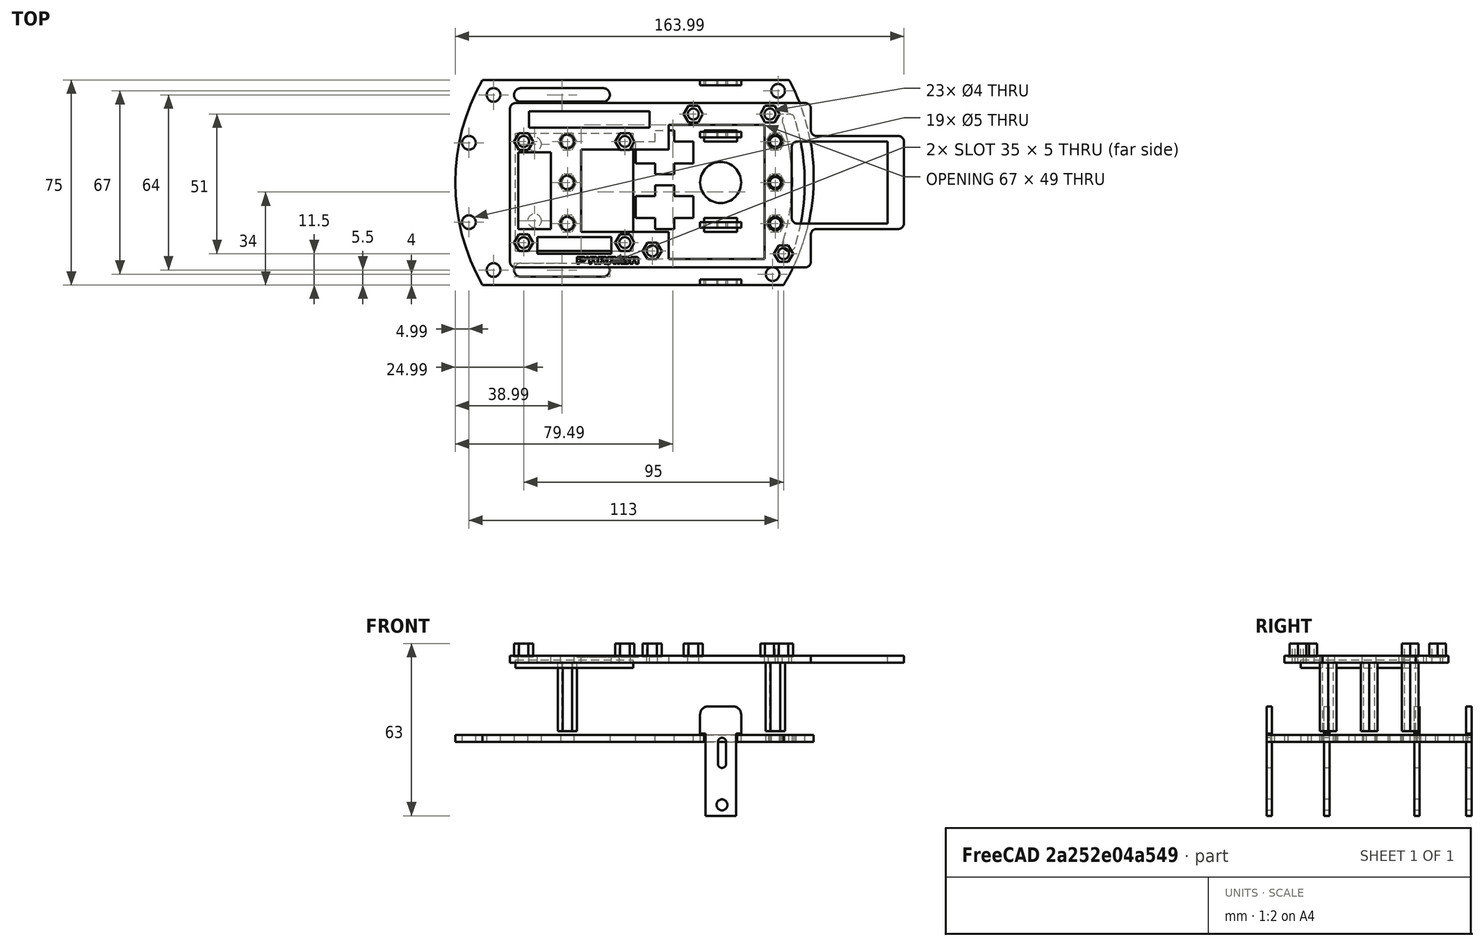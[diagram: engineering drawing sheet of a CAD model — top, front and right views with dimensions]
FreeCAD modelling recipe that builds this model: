
FCSTD DOCUMENT  (FreeCAD 0.17R13541 (Git))
Label: masayloChino2020
License: All rights reserved
LicenseURL: http://en.wikipedia.org/wiki/All_rights_reserved
objects: Part::Cylinder×41, Part::Cut×30, Part::Box×21, Part::Feature×18, Part::MultiFuse×16, Part::Prism×15, Part::Extrusion×15, Part::Fillet×6, Mesh::Feature×4, Sketcher::SketchObject×1, PartDesign::Pad×1, PartDesign::Body×1, Part::FeaturePython×1
note: 167 computed .brp shape members not serialized (recipe doc carries the construction recipe); baked Part::Feature solids carry a one-line shape summary decoded from their .brp

FEATURE [Sketcher::SketchObject] Sketch
  MapMode = 5
  Support = -> [XY_Plane]
  sketch-geometry (71):
    g0: LineSegment StartX=0 StartY=37.5 StartZ=0 EndX=81 EndY=37.5 EndZ=0
    g1: LineSegment StartX=110 StartY=-37.5 StartZ=0 EndX=93 EndY=-37.5 EndZ=0
    g2: Circle CenterX=4 CenterY=-32 CenterZ=0 NormalX=0 NormalY=0 NormalZ=1 AngleXU=0 Radius=2.5
    g3: ArcOfCircle CenterX=14 CenterY=-32 CenterZ=0 NormalX=0 NormalY=0 NormalZ=1 AngleXU=0 Radius=2.5 StartAngle=1.5708 EndAngle=4.71239
    g4: ArcOfCircle CenterX=44 CenterY=-32 CenterZ=0 NormalX=0 NormalY=0 NormalZ=1 AngleXU=0 Radius=2.5 StartAngle=4.71239 EndAngle=7.85398
    g5: LineSegment StartX=14 StartY=-34.5 StartZ=0 EndX=44 EndY=-34.5 EndZ=0
    g6: LineSegment StartX=14 StartY=-29.5 StartZ=0 EndX=44 EndY=-29.5 EndZ=0
    g7: Circle CenterX=-5 CenterY=-14.5 CenterZ=0 NormalX=0 NormalY=0 NormalZ=1 AngleXU=0 Radius=2.5
    g8: Circle CenterX=-5 CenterY=14.5 CenterZ=0 NormalX=0 NormalY=0 NormalZ=1 AngleXU=0 Radius=2.5
    g9: Circle CenterX=19 CenterY=-14 CenterZ=0 NormalX=0 NormalY=0 NormalZ=1 AngleXU=0 Radius=2.5
    g10: Circle CenterX=31 CenterY=-15 CenterZ=0 NormalX=0 NormalY=0 NormalZ=1 AngleXU=0 Radius=2.5
    g11: ArcOfCircle CenterX=65.3673 CenterY=0 CenterZ=0 NormalX=0 NormalY=0 NormalZ=1 AngleXU=0 Radius=75.36 StartAngle=2.62075 EndAngle=3.66244
    g12: ArcOfCircle CenterX=14 CenterY=32 CenterZ=0 NormalX=0 NormalY=0 NormalZ=1 AngleXU=0 Radius=2.5 StartAngle=1.5708 EndAngle=4.71239
    g13: ArcOfCircle CenterX=44 CenterY=32 CenterZ=0 NormalX=0 NormalY=0 NormalZ=1 AngleXU=0 Radius=2.5 StartAngle=4.71239 EndAngle=7.85398
    g14: LineSegment StartX=14 StartY=29.5 StartZ=0 EndX=44 EndY=29.5 EndZ=0
    g15: LineSegment StartX=14 StartY=34.5 StartZ=0 EndX=44 EndY=34.5 EndZ=0
    g16: Circle CenterX=4 CenterY=32 CenterZ=0 NormalX=0 NormalY=0 NormalZ=1 AngleXU=0 Radius=2.5
    g17: Circle CenterX=31 CenterY=0 CenterZ=0 NormalX=0 NormalY=0 NormalZ=1 AngleXU=0 Radius=2.5
    g18: Circle CenterX=31 CenterY=15 CenterZ=0 NormalX=0 NormalY=0 NormalZ=1 AngleXU=0 Radius=2.5
    g19: LineSegment StartX=56 StartY=-13 StartZ=0 EndX=63 EndY=-13 EndZ=0
    g20: LineSegment StartX=77 StartY=-13 StartZ=0 EndX=77 EndY=-5 EndZ=0
    g21: LineSegment StartX=77 StartY=-5 StartZ=0 EndX=70 EndY=-5 EndZ=0
    g22: LineSegment StartX=56 StartY=-5 StartZ=0 EndX=56 EndY=-13 EndZ=0
    g23: LineSegment StartX=63 StartY=-1 StartZ=0 EndX=70 EndY=-1 EndZ=0
    g24: LineSegment StartX=70 StartY=-1 StartZ=0 EndX=70 EndY=-5 EndZ=0
    g25: LineSegment StartX=70 StartY=-17 StartZ=0 EndX=63 EndY=-17 EndZ=0
    g26: LineSegment StartX=63 StartY=-17 StartZ=0 EndX=63 EndY=-13 EndZ=0
    g27: LineSegment StartX=63 StartY=-5 StartZ=0 EndX=56 EndY=-5 EndZ=0
    g28: LineSegment StartX=63 StartY=-5 StartZ=0 EndX=63 EndY=-1 EndZ=0
    g29: LineSegment StartX=70 StartY=-13 StartZ=0 EndX=70 EndY=-17 EndZ=0
    g30: LineSegment StartX=70 StartY=-13 StartZ=0 EndX=77 EndY=-13 EndZ=0
    g31: Circle CenterX=87 CenterY=0 CenterZ=0 NormalX=0 NormalY=0 NormalZ=1 AngleXU=0 Radius=7.5
    g32: LineSegment StartX=63 StartY=19 StartZ=0 EndX=70 EndY=19 EndZ=0
    g33: LineSegment StartX=70 StartY=19 StartZ=0 EndX=70 EndY=15 EndZ=0
    g34: LineSegment StartX=70 StartY=3 StartZ=0 EndX=63 EndY=3 EndZ=0
    g35: LineSegment StartX=63 StartY=3 StartZ=0 EndX=63 EndY=7 EndZ=0
    g36: LineSegment StartX=56 StartY=15 StartZ=0 EndX=63 EndY=15 EndZ=0
    g37: LineSegment StartX=77 StartY=15 StartZ=0 EndX=77 EndY=7 EndZ=0
    g38: LineSegment StartX=77 StartY=7 StartZ=0 EndX=70 EndY=7 EndZ=0
    g39: LineSegment StartX=56 StartY=7 StartZ=0 EndX=56 EndY=15 EndZ=0
    g40: LineSegment StartX=63 StartY=15 StartZ=0 EndX=63 EndY=19 EndZ=0
    g41: LineSegment StartX=70 StartY=7 StartZ=0 EndX=70 EndY=3 EndZ=0
    g42: LineSegment StartX=63 StartY=7 StartZ=0 EndX=56 EndY=7 EndZ=0
    g43: LineSegment StartX=70 StartY=15 StartZ=0 EndX=77 EndY=15 EndZ=0
    g44: LineSegment StartX=81 StartY=-13 StartZ=0 EndX=93 EndY=-13 EndZ=0
    g45: LineSegment StartX=93 StartY=-13 StartZ=0 EndX=93 EndY=-18 EndZ=0
    g46: LineSegment StartX=93 StartY=-18 StartZ=0 EndX=81 EndY=-18 EndZ=0
    g47: LineSegment StartX=81 StartY=-18 StartZ=0 EndX=81 EndY=-13 EndZ=0
    g48: LineSegment StartX=81 StartY=19 StartZ=0 EndX=93 EndY=19 EndZ=0
    g49: LineSegment StartX=93 StartY=19 StartZ=0 EndX=93 EndY=15 EndZ=0
    g50: LineSegment StartX=93 StartY=15 StartZ=0 EndX=81 EndY=15 EndZ=0
    g51: LineSegment StartX=81 StartY=15 StartZ=0 EndX=81 EndY=19 EndZ=0
    g52: Circle CenterX=107 CenterY=0 CenterZ=0 NormalX=0 NormalY=0 NormalZ=1 AngleXU=0 Radius=2
    g53: Circle CenterX=107 CenterY=-15 CenterZ=0 NormalX=0 NormalY=0 NormalZ=1 AngleXU=0 Radius=2.5
    g54: Circle CenterX=107 CenterY=15 CenterZ=0 NormalX=0 NormalY=0 NormalZ=1 AngleXU=0 Radius=2.5
    g55: Circle CenterX=106 CenterY=-33.5 CenterZ=0 NormalX=0 NormalY=0 NormalZ=1 AngleXU=0 Radius=2.5
    g56: Circle CenterX=108 CenterY=33.5 CenterZ=0 NormalX=0 NormalY=0 NormalZ=1 AngleXU=0 Radius=2.5
    g57: ArcOfCircle CenterX=45.6636 CenterY=1.7423 CenterZ=0 NormalX=0 NormalY=0 NormalZ=1 AngleXU=0 Radius=75.36 StartAngle=5.73548 EndAngle=6.77757
    g58: ArcOfCircle CenterX=112 CenterY=22.5 CenterZ=0 NormalX=0 NormalY=0 NormalZ=1 AngleXU=0 Radius=2.5 StartAngle=0.75994 EndAngle=3.89869
    g59: ArcOfCircle CenterX=112 CenterY=-22.5 CenterZ=0 NormalX=0 NormalY=0 NormalZ=1 AngleXU=0 Radius=2.5 StartAngle=2.5229 EndAngle=6.37272
    g60: ArcOfCircle CenterX=39.6948 CenterY=-0.112448 CenterZ=0 NormalX=0 NormalY=0 NormalZ=1 AngleXU=0 Radius=78.01 StartAngle=5.9951 EndAngle=6.60042
    g61: ArcOfCircle CenterX=38.1627 CenterY=0.243776 CenterZ=0 NormalX=0 NormalY=0 NormalZ=1 AngleXU=0 Radius=74.8917 StartAngle=5.99488 EndAngle=6.561
    g62: LineSegment StartX=81 StartY=-35.5 StartZ=0 EndX=93 EndY=-35.5 EndZ=0
    g63: LineSegment StartX=93 StartY=-35.5 StartZ=0 EndX=93 EndY=-37.5 EndZ=0
    g64: LineSegment StartX=81 StartY=-37.5 StartZ=0 EndX=81 EndY=-35.5 EndZ=0
    g65: LineSegment StartX=81 StartY=-37.5 StartZ=0 EndX=0 EndY=-37.5 EndZ=0
    g66: LineSegment StartX=93 StartY=37.5 StartZ=0 EndX=93 EndY=35.5 EndZ=0
    g67: LineSegment StartX=93 StartY=35.5 StartZ=0 EndX=81 EndY=35.5 EndZ=0
    g68: LineSegment StartX=81 StartY=35.5 StartZ=0 EndX=81 EndY=37.5 EndZ=0
    g69: LineSegment StartX=93 StartY=37.5 StartZ=0 EndX=112 EndY=37.5 EndZ=0
    g70: Circle CenterX=19 CenterY=14 CenterZ=0 NormalX=0 NormalY=0 NormalZ=1 AngleXU=0 Radius=2.5
  constraints (200):
    c: Horizontal(g0)
    c: Horizontal(g1)
    c: DistanceX(g65,g1) = 110
    c: DistanceY(g1,g69) = 75
    c: PointOnObject(g0,g-2)
    c: Radius(g2) = 2.5
    c: DistanceY(g65,g2) = 5.5
    c: DistanceX(g2) = 4
    c: Tangent(g3,g6) = 1.5708
    c: Tangent(g3,g5) = -1.5708
    c: Tangent(g5,g4) = -1.5708
    c: Tangent(g6,g4) = 1.5708
    c: Horizontal(g5)
    c: Equal(g3,g4)
    c: Radius(g3) = 2.5
    c: DistanceY(g65,g3) = 5.5
    c: DistanceX(g3,g4) = 30
    c: DistanceX(g2,g3) = 10
    c: Radius(g7) = 2.5
    c: DistanceY(g65,g7) = 23
    c: DistanceX(g7,g65) = 5
    c: Radius(g8) = 2.5
    c: DistanceY(g8,g0) = 23
    c: DistanceX(g8,g0) = 5
    c: Radius(g9) = 2.5
    c: DistanceY(g2,g9) = 18
    c: DistanceX(g2,g9) = 15
    c: Radius(g10) = 2.5
    c: DistanceX(g9,g10) = 12
    c: DistanceY(g3,g10) = 17
    c: DistanceY(g65,g-1) = 37.5
    c: Coincident(g11,g65)
    c: Radius(g11) = 75.36
    c: Coincident(g11,g0)
    c: PointOnObject(g65,g-2)
    c: Tangent(g12,g15) = 1.5708
    c: Tangent(g12,g14) = -1.5708
    c: Tangent(g14,g13) = -1.5708
    c: Tangent(g15,g13) = 1.5708
    c: Horizontal(g14)
    c: Equal(g12,g13)
    c: Radius(g13) = 2.5
    c: DistanceX(g12,g13) = 30
    c: Radius(g16) = 2.5
    c: DistanceX(g0,g16) = 4
    c: DistanceY(g16,g0) = 5.5
    c: DistanceY(g12,g0) = 5.5
    c: DistanceX(g16,g12) = 10
    c: Radius(g18) = 2.5
    c: Radius(g17) = 2.5
    c: DistanceX(g9,g17) = 12
    c: DistanceY(g10,g17) = 15
    c: DistanceX(g9,g18) = 12
    c: DistanceY(g17,g18) = 15
    c: Coincident(g30,g20)
    c: Coincident(g20,g21)
    c: Coincident(g27,g22)
    c: Coincident(g22,g19)
    c: Horizontal(g19)
    c: Horizontal(g21)
    c: Vertical(g20)
    c: Vertical(g22)
    c: DistanceX(g4,g27) = 12
    c: DistanceX(g27,g20) = 21
    c: DistanceY(g20,g20) = 8
    c: DistanceY(g4,g19) = 19
    c: Coincident(g23,g24)
    c: Coincident(g29,g25)
    c: Coincident(g25,g26)
    c: Coincident(g28,g23)
    c: Horizontal(g23)
    c: Horizontal(g25)
    c: Vertical(g24)
    c: Vertical(g26)
    c: DistanceX(g19,g25) = 7
    c: DistanceY(g25,g19) = 4
    c: DistanceY(g27,g23) = 4
    c: DistanceX(g23,g23) = 7
    c: Tangent(g21,g27)
    c: Coincident(g28,g27)
    c: Tangent(g26,g28)
    c: Coincident(g24,g21)
    c: Tangent(g24,g29)
    c: Coincident(g19,g26)
    c: Coincident(g30,g29)
    c: Tangent(g19,g30)
    c: Radius(g31) = 7.5
    c: PointOnObject(g31,g-1)
    c: DistanceX(g20,g31) = 10
    c: Coincident(g32,g33)
    c: Coincident(g41,g34)
    c: Coincident(g34,g35)
    c: Coincident(g40,g32)
    c: Horizontal(g32)
    c: Horizontal(g34)
    c: Vertical(g33)
    c: Vertical(g35)
    c: Coincident(g43,g37)
    c: Coincident(g37,g38)
    c: Coincident(g42,g39)
    c: Coincident(g39,g36)
    c: Horizontal(g36)
    c: Horizontal(g38)
    c: Vertical(g37)
    c: Vertical(g39)
    c: Tangent(g35,g40)
    c: Tangent(g33,g41)
    c: Coincident(g38,g41)
    c: Coincident(g42,g35)
    c: Tangent(g38,g42)
    c: Coincident(g36,g40)
    c: Coincident(g43,g33)
    c: Tangent(g36,g43)
    c: DistanceX(g42,g42) = 7
    c: DistanceY(g35,g35) = 4
    c: DistanceX(g34,g23) = 0
    c: DistanceY(g23,g34) = 4
    c: DistanceX(g34,g23) = 0
    c: DistanceX(g38,g38) = 7
    c: DistanceY(g37,g37) = 8
    c: DistanceY(g33,g32) = 4
    c: Coincident(g44,g45)
    c: Coincident(g45,g46)
    c: Coincident(g46,g47)
    c: Coincident(g47,g44)
    c: Horizontal(g44)
    c: Horizontal(g46)
    c: Vertical(g45)
    c: Vertical(g47)
    c: DistanceX(g46,g46) = 12
    c: DistanceY(g45,g45) = 5
    c: DistanceX(g20,g44) = 4
    c: DistanceY(g20,g44) = 0
    c: Coincident(g48,g49)
    c: Coincident(g49,g50)
    c: Coincident(g50,g51)
    c: Coincident(g51,g48)
    c: Horizontal(g48)
    c: Horizontal(g50)
    c: Vertical(g49)
    c: Vertical(g51)
    c: DistanceX(g50,g50) = 12
    c: DistanceY(g49,g49) = 4
    c: DistanceY(g37,g50) = 0
    c: DistanceX(g37,g50) = 4
    c: PointOnObject(g52,g-1)
    c: Radius(g52) = 2
    c: DistanceX(g31,g52) = 20
    c: Radius(g53) = 2.5
    c: Radius(g54) = 2.5
    c: DistanceX(g53,g52) = 0
    c: DistanceX(g54,g52) = 0
    c: DistanceY(g52,g54) = 15
    c: DistanceY(g53,g52) = 15
    c: Radius(g55) = 2.5
    c: DistanceX(g55,g1) = 4
    c: DistanceY(g1,g55) = 4
    c: Radius(g56) = 2.5
    c: DistanceX(g56,g69) = 4
    c: DistanceY(g56,g69) = 4
    c: Coincident(g57,g69)
    c: Coincident(g57,g1)
    c: DistanceX(g0,g69) = 112
    c: Radius(g57) = 75.36
    c: Radius(g59) = 2.5
    c: Radius(g58) = 2.5
    c: DistanceY(g54,g58) = 7.5
    c: DistanceX(g54,g58) = 5
    c: DistanceY(g59,g53) = 7.5
    c: DistanceX(g53,g59) = 5
    c: Coincident(g58,g60)
    c: Coincident(g58,g61)
    c: Coincident(g59,g61)
    c: Coincident(g59,g60)
    c: Coincident(g62,g63)
    c: Coincident(g64,g62)
    c: Horizontal(g62)
    c: Vertical(g63)
    c: Vertical(g64)
    c: DistanceX(g62,g46) = 0
    c: DistanceX(g45,g62) = 0
    c: DistanceY(g64,g62) = 2
    c: Coincident(g1,g63)
    c: PointOnObject(g65,g64)
    c: Tangent(g1,g65)
    c: Coincident(g66,g67)
    c: Coincident(g67,g68)
    c: Horizontal(g67)
    c: Vertical(g66)
    c: Vertical(g68)
    c: PointOnObject(g66,g0)
    c: DistanceY(g66,g66) = 2
    c: DistanceX(g48,g66) = 0
    c: DistanceX(g67,g48) = 0
    c: PointOnObject(g0,g68)
    c: PointOnObject(g69,g66)
    c: Tangent(g0,g69)
    c: Radius(g70) = 2.5
    c: DistanceX(g70,g18) = 12
    c: DistanceY(g70,g18) = 1
FEATURE [PartDesign::Pad] Pad
  Length = 2.5
  Length2 = 100
  Profile = -> Sketch
  Type = 0
FEATURE [PartDesign::Body] Body
  Group = -> [Sketch,Pad]
  Origin = -> Origin
  Tip = -> Pad
FEATURE [Mesh::Feature] nano_expansion_shield
  Placement = pos=(113,-29,35) rot=(0,0,1;1.5708rad)
FEATURE [Part::Box] Box  label="Cubo"
  AttacherType = Attacher::AttachEngine3D
  Height = 2.5
  Length = 110
  Placement = pos=(10,-31,25) rot=(0,0,1;0rad)
  Width = 60
FEATURE [Part::Cylinder] Cylinder  label="Cilindro"
  Angle = 360
  AttacherType = Attacher::AttachEngine3D
  Height = 50
  Placement = pos=(31,0,-4) rot=(0,0,1;0rad)
  Radius = 2.5
FEATURE [Part::Cylinder] Cylinder001  label="Cilindro001"
  Angle = 360
  AttacherType = Attacher::AttachEngine3D
  Height = 50
  Placement = pos=(31,-15,-4) rot=(0,0,1;0rad)
  Radius = 2.5
FEATURE [Part::Cylinder] Cylinder002  label="Cilindro002"
  Angle = 360
  AttacherType = Attacher::AttachEngine3D
  Height = 50
  Placement = pos=(31,15,-4) rot=(0,0,1;0rad)
  Radius = 2.5
FEATURE [Part::Cylinder] Cylinder003  label="Cilindro003"
  Angle = 360
  AttacherType = Attacher::AttachEngine3D
  Height = 50
  Placement = pos=(107,15,-4) rot=(0,0,1;0rad)
  Radius = 2.5
FEATURE [Part::Cylinder] Cylinder004  label="Cilindro004"
  Angle = 360
  AttacherType = Attacher::AttachEngine3D
  Height = 50
  Placement = pos=(107,0,-4) rot=(0,0,1;0rad)
  Radius = 2.5
FEATURE [Part::Cylinder] Cylinder005  label="Cilindro005"
  Angle = 360
  AttacherType = Attacher::AttachEngine3D
  Height = 50
  Placement = pos=(107,-15,-4) rot=(0,0,1;0rad)
  Radius = 2.5
FEATURE [Part::MultiFuse] Fusion
  Shapes = -> [Cylinder,Cylinder001,Cylinder002,Cylinder003,Cylinder004,Cylinder005]
FEATURE [Part::Cut] Cut
  Base = -> Box
  Tool = -> Fusion
FEATURE [Part::Cylinder] Cylinder006  label="Cilindro006"
  Angle = 360
  AttacherType = Attacher::AttachEngine3D
  Height = 10
  Placement = pos=(3,3,47) rot=(0,0,1;0rad)
  Radius = 2
FEATURE [Part::Cylinder] Cylinder007  label="Cilindro007"
  Angle = 360
  AttacherType = Attacher::AttachEngine3D
  Height = 10
  Placement = pos=(3,40,47) rot=(0,0,1;0rad)
  Radius = 2
FEATURE [Part::Cylinder] Cylinder008  label="Cilindro008"
  Angle = 360
  AttacherType = Attacher::AttachEngine3D
  Height = 10
  Placement = pos=(40,3,47) rot=(0,0,1;0rad)
  Radius = 2
FEATURE [Part::Cylinder] Cylinder009  label="Cilindro009"
  Angle = 360
  AttacherType = Attacher::AttachEngine3D
  Height = 10
  Placement = pos=(40,40,47) rot=(0,0,1;0rad)
  Radius = 2
FEATURE [Part::Box] Box001  label="l298n"
  AttacherType = Attacher::AttachEngine3D
  Height = 3
  Length = 43
  Placement = pos=(12,-25,27) rot=(0,0,1;0rad)
  Width = 43
FEATURE [Part::MultiFuse] Fusion001  label="TALADROSL298N"
  Placement = pos=(12,-25,-27) rot=(0,0,1;0rad)
  Shapes = -> [Cylinder006,Cylinder007,Cylinder009,Cylinder008]
FEATURE [Part::Cylinder] Cylinder010  label="Cilindro010"
  Angle = 360
  AttacherType = Attacher::AttachEngine3D
  Height = 10
  Placement = pos=(31,-16,-2) rot=(0,0,1;0rad)
  Radius = 2
FEATURE [Part::Cylinder] Cylinder011  label="Cilindro011"
  Angle = 360
  AttacherType = Attacher::AttachEngine3D
  Height = 10
  Placement = pos=(79,-17,-2) rot=(0,0,1;0rad)
  Radius = 2
FEATURE [Part::Cylinder] Cylinder012  label="Cilindro012"
  Angle = 360
  AttacherType = Attacher::AttachEngine3D
  Height = 10
  Placement = pos=(74,34,-2) rot=(0,0,1;0rad)
  Radius = 2
FEATURE [Part::Cylinder] Cylinder013  label="Cilindro013"
  Angle = 360
  AttacherType = Attacher::AttachEngine3D
  Height = 10
  Placement = pos=(46,34,-2) rot=(0,0,1;0rad)
  Radius = 2
FEATURE [Part::MultiFuse] Fusion002  label="taladrosNanoShield"
  Placement = pos=(31,-9,24) rot=(0,0,1;0rad)
  Shapes = -> [Cylinder013,Cylinder011,Cylinder010,Cylinder012]
FEATURE [Part::MultiFuse] Fusion003  label="TALADROSPISO2"
  Shapes = -> [Fusion001,Fusion002]
FEATURE [Part::Cut] Cut001
  Base = -> Cut
  Tool = -> Fusion003
FEATURE [Part::Box] Box002  label="Cubo001"
  AttacherType = Attacher::AttachEngine3D
  Height = 10
  Length = 67
  Placement = pos=(36,-18,20) rot=(0,0,1;0rad)
  Width = 30
FEATURE [Part::Box] Box003  label="Cubo002"
  AttacherType = Attacher::AttachEngine3D
  Height = 10
  Length = 35
  Placement = pos=(68,-28,20) rot=(0,0,1;0rad)
  Width = 49
FEATURE [Part::Box] Box004  label="Cubo003"
  AttacherType = Attacher::AttachEngine3D
  Height = 10
  Length = 12
  Placement = pos=(13,-17,20) rot=(0,0,1;0rad)
  Width = 28
FEATURE [Part::Box] Box005  label="Cubo004"
  AttacherType = Attacher::AttachEngine3D
  Height = 10
  Length = 44
  Placement = pos=(17,20,20) rot=(0,0,1;0rad)
  Width = 6
FEATURE [Part::Box] Box006  label="Cubo005"
  AttacherType = Attacher::AttachEngine3D
  Height = 10
  Length = 27
  Placement = pos=(20,-26,20) rot=(0,0,1;0rad)
  Width = 6
FEATURE [Part::MultiFuse] Fusion004  label="agujerosPiso2"
  Shapes = -> [Box002,Box003,Box004,Box005,Box006]
FEATURE [Part::Cut] Cut002
  Base = -> Cut001
  Tool = -> Fusion004
FEATURE [Part::Fillet] Fillet  label="piso2"
  Base = -> Cut002
  Edges = 4 edges r=2: [Edge1,Edge3,Edge6,Edge47]
  Placement = pos=(0,0,4) rot=(0,0,1;0rad)
FEATURE [Part::Cylinder] Cylinder014  label="Cilindro014"
  Angle = 360
  AttacherType = Attacher::AttachEngine3D
  Height = 30
  Placement = pos=(0,0,-2) rot=(0,0,1;0rad)
  Radius = 2
FEATURE [Part::Prism] Prism  label="Prisma"
  AttacherType = Attacher::AttachEngine3D
  Circumradius = 3.5
  Height = 25
  Polygon = 6
FEATURE [Part::Cut] Cut003  label="separador"
  Base = -> Prism
  Placement = pos=(31,0,4) rot=(0,0,1;0rad)
  Tool = -> Cylinder014
FEATURE [Part::Cylinder] Cylinder015  label="Cilindro015"
  Angle = 360
  AttacherType = Attacher::AttachEngine3D
  Height = 30
  Placement = pos=(0,0,-2) rot=(0,0,1;0rad)
  Radius = 2
FEATURE [Part::Prism] Prism001  label="Prisma001"
  AttacherType = Attacher::AttachEngine3D
  Circumradius = 3.5
  Height = 25
  Polygon = 6
FEATURE [Part::Cut] Cut004  label="separador001"
  Base = -> Prism001
  Placement = pos=(31,15,4) rot=(0,0,1;0rad)
  Tool = -> Cylinder015
FEATURE [Part::Cylinder] Cylinder016  label="Cilindro016"
  Angle = 360
  AttacherType = Attacher::AttachEngine3D
  Height = 30
  Placement = pos=(0,0,-2) rot=(0,0,1;0rad)
  Radius = 2
FEATURE [Part::Prism] Prism002  label="Prisma002"
  AttacherType = Attacher::AttachEngine3D
  Circumradius = 3.5
  Height = 25
  Polygon = 6
FEATURE [Part::Cut] Cut005  label="separador002"
  Base = -> Prism002
  Placement = pos=(31,-15,4) rot=(0,0,1;0rad)
  Tool = -> Cylinder016
FEATURE [Part::Prism] Prism003  label="Prisma003"
  AttacherType = Attacher::AttachEngine3D
  Circumradius = 3.5
  Height = 25
  Polygon = 6
FEATURE [Part::Cylinder] Cylinder017  label="Cilindro017"
  Angle = 360
  AttacherType = Attacher::AttachEngine3D
  Height = 30
  Placement = pos=(0,0,-2) rot=(0,0,1;0rad)
  Radius = 2
FEATURE [Part::Cut] Cut006  label="separador003"
  Base = -> Prism003
  Placement = pos=(107,-15,4) rot=(0,0,1;0rad)
  Tool = -> Cylinder017
FEATURE [Part::Cylinder] Cylinder018  label="Cilindro018"
  Angle = 360
  AttacherType = Attacher::AttachEngine3D
  Height = 30
  Placement = pos=(0,0,-2) rot=(0,0,1;0rad)
  Radius = 2
FEATURE [Part::Prism] Prism004  label="Prisma004"
  AttacherType = Attacher::AttachEngine3D
  Circumradius = 3.5
  Height = 25
  Polygon = 6
FEATURE [Part::Cut] Cut007  label="separador004"
  Base = -> Prism004
  Placement = pos=(107,0,4) rot=(0,0,1;0rad)
  Tool = -> Cylinder018
FEATURE [Part::Cylinder] Cylinder019  label="Cilindro019"
  Angle = 360
  AttacherType = Attacher::AttachEngine3D
  Height = 30
  Placement = pos=(0,0,-2) rot=(0,0,1;0rad)
  Radius = 2
FEATURE [Part::Prism] Prism005  label="Prisma005"
  AttacherType = Attacher::AttachEngine3D
  Circumradius = 3.5
  Height = 25
  Polygon = 6
FEATURE [Part::Cut] Cut008  label="separador005"
  Base = -> Prism005
  Placement = pos=(107,15,4) rot=(0,0,1;0rad)
  Tool = -> Cylinder019
FEATURE [Part::Prism] Prism006  label="Prisma006"
  AttacherType = Attacher::AttachEngine3D
  Circumradius = 3.5
  Height = 25
  Polygon = 6
FEATURE [Part::Cylinder] Cylinder020  label="Cilindro020"
  Angle = 360
  AttacherType = Attacher::AttachEngine3D
  Height = 30
  Placement = pos=(0,0,-2) rot=(0,0,1;0rad)
  Radius = 2
FEATURE [Part::Cut] Cut009  label="separador006"
  Base = -> Prism006
  Placement = pos=(31,0,4) rot=(0,0,1;0rad)
  Tool = -> Cylinder020
FEATURE [Part::Box] Box007  label="Cubo006"
  AttacherType = Attacher::AttachEngine3D
  Height = 33
  Length = 11.2
  Placement = pos=(81.5,35.5,-27) rot=(0,0,1;0rad)
  Width = 2
FEATURE [Part::Cylinder] Cylinder022  label="Cilindro022"
  Angle = 360
  AttacherType = Attacher::AttachEngine3D
  Height = 10
  Placement = pos=(87.5,41.5,-8) rot=(1,0,0;1.5708rad)
  Radius = 1.5
FEATURE [Part::Box] Box009  label="Cubo008"
  AttacherType = Attacher::AttachEngine3D
  Height = 8
  Length = 3
  Placement = pos=(86,32,-8) rot=(0,0,1;0rad)
  Width = 10
FEATURE [Part::Cylinder] Cylinder021  label="Cilindro021"
  Angle = 360
  AttacherType = Attacher::AttachEngine3D
  Height = 10
  Placement = pos=(87.5,41.5,0) rot=(1,0,0;1.5708rad)
  Radius = 1.5
FEATURE [Part::Cylinder] Cylinder023  label="Cilindro023"
  Angle = 360
  AttacherType = Attacher::AttachEngine3D
  Height = 10
  Placement = pos=(87.5,41.5,-23) rot=(1,0,0;1.5708rad)
  Radius = 2
FEATURE [Part::MultiFuse] Fusion006
  Shapes = -> [Box009,Cylinder022,Cylinder021,Cylinder023]
FEATURE [Part::Box] Box008  label="Cubo007"
  AttacherType = Attacher::AttachEngine3D
  Height = 10
  Length = 15
  Placement = pos=(79.5,35.5,3) rot=(0,0,1;0rad)
  Width = 2
FEATURE [Part::MultiFuse] Fusion005
  Shapes = -> [Box007,Box008]
FEATURE [Part::Fillet] Fillet001
  Base = -> Fusion005
  Edges = 2 edges r=3: [Edge30,Edge32]
FEATURE [Part::Cut] Cut010  label="colocador"
  Base = -> Fillet001
  Tool = -> Fusion006
FEATURE [Part::Box] Box010  label="Cubo009"
  AttacherType = Attacher::AttachEngine3D
  Height = 33
  Length = 11.2
  Placement = pos=(81.5,35.5,-27) rot=(0,0,1;0rad)
  Width = 2
FEATURE [Part::Cylinder] Cylinder024  label="Cilindro024"
  Angle = 360
  AttacherType = Attacher::AttachEngine3D
  Height = 10
  Placement = pos=(87.5,41.5,0) rot=(1,0,0;1.5708rad)
  Radius = 1.5
FEATURE [Part::Box] Box011  label="Cubo010"
  AttacherType = Attacher::AttachEngine3D
  Height = 10
  Length = 15
  Placement = pos=(79.5,35.5,3) rot=(0,0,1;0rad)
  Width = 2
FEATURE [Part::MultiFuse] Fusion007
  Shapes = -> [Box010,Box011]
FEATURE [Part::Fillet] Fillet002
  Base = -> Fusion007
  Edges = 2 edges r=3: [Edge30,Edge32]
FEATURE [Part::Cylinder] Cylinder025  label="Cilindro025"
  Angle = 360
  AttacherType = Attacher::AttachEngine3D
  Height = 10
  Placement = pos=(87.5,41.5,-8) rot=(1,0,0;1.5708rad)
  Radius = 1.5
FEATURE [Part::Cylinder] Cylinder026  label="Cilindro026"
  Angle = 360
  AttacherType = Attacher::AttachEngine3D
  Height = 10
  Placement = pos=(87.5,41.5,-23) rot=(1,0,0;1.5708rad)
  Radius = 2
FEATURE [Part::Box] Box012  label="Cubo011"
  AttacherType = Attacher::AttachEngine3D
  Height = 8
  Length = 3
  Placement = pos=(86,32,-8) rot=(0,0,1;0rad)
  Width = 10
FEATURE [Part::MultiFuse] Fusion008
  Shapes = -> [Box012,Cylinder025,Cylinder024,Cylinder026]
FEATURE [Part::Cut] Cut011  label="colocador001"
  Base = -> Fillet002
  Placement = pos=(0,-19,0) rot=(0,0,1;0rad)
  Tool = -> Fusion008
FEATURE [Part::Box] Box013  label="Cubo012"
  AttacherType = Attacher::AttachEngine3D
  Height = 33
  Length = 11.2
  Placement = pos=(81.5,35.5,-27) rot=(0,0,1;0rad)
  Width = 2
FEATURE [Part::Cylinder] Cylinder027  label="Cilindro027"
  Angle = 360
  AttacherType = Attacher::AttachEngine3D
  Height = 10
  Placement = pos=(87.5,41.5,0) rot=(1,0,0;1.5708rad)
  Radius = 1.5
FEATURE [Part::Box] Box014  label="Cubo013"
  AttacherType = Attacher::AttachEngine3D
  Height = 10
  Length = 15
  Placement = pos=(79.5,35.5,3) rot=(0,0,1;0rad)
  Width = 2
FEATURE [Part::MultiFuse] Fusion009
  Shapes = -> [Box013,Box014]
FEATURE [Part::Fillet] Fillet003
  Base = -> Fusion009
  Edges = 2 edges r=3: [Edge30,Edge32]
FEATURE [Part::Cylinder] Cylinder028  label="Cilindro028"
  Angle = 360
  AttacherType = Attacher::AttachEngine3D
  Height = 10
  Placement = pos=(87.5,41.5,-8) rot=(1,0,0;1.5708rad)
  Radius = 1.5
FEATURE [Part::Cylinder] Cylinder029  label="Cilindro029"
  Angle = 360
  AttacherType = Attacher::AttachEngine3D
  Height = 10
  Placement = pos=(87.5,41.5,-23) rot=(1,0,0;1.5708rad)
  Radius = 2
FEATURE [Part::Box] Box015  label="Cubo014"
  AttacherType = Attacher::AttachEngine3D
  Height = 8
  Length = 3
  Placement = pos=(86,32,-8) rot=(0,0,1;0rad)
  Width = 10
FEATURE [Part::MultiFuse] Fusion010
  Shapes = -> [Box015,Cylinder028,Cylinder027,Cylinder029]
FEATURE [Part::Cut] Cut012  label="colocador002"
  Base = -> Fillet003
  Placement = pos=(0,-52,0) rot=(0,0,1;0rad)
  Tool = -> Fusion010
FEATURE [Part::Cylinder] Cylinder030  label="Cilindro030"
  Angle = 360
  AttacherType = Attacher::AttachEngine3D
  Height = 10
  Placement = pos=(87.5,41.5,-8) rot=(1,0,0;1.5708rad)
  Radius = 1.5
FEATURE [Part::Box] Box016  label="Cubo015"
  AttacherType = Attacher::AttachEngine3D
  Height = 8
  Length = 3
  Placement = pos=(86,32,-8) rot=(0,0,1;0rad)
  Width = 10
FEATURE [Part::Box] Box017  label="Cubo016"
  AttacherType = Attacher::AttachEngine3D
  Height = 33
  Length = 11.2
  Placement = pos=(81.5,35.5,-27) rot=(0,0,1;0rad)
  Width = 2
FEATURE [Part::Box] Box018  label="Cubo017"
  AttacherType = Attacher::AttachEngine3D
  Height = 10
  Length = 15
  Placement = pos=(79.5,35.5,3) rot=(0,0,1;0rad)
  Width = 2
FEATURE [Part::Cylinder] Cylinder031  label="Cilindro031"
  Angle = 360
  AttacherType = Attacher::AttachEngine3D
  Height = 10
  Placement = pos=(87.5,41.5,-23) rot=(1,0,0;1.5708rad)
  Radius = 2
FEATURE [Part::Cylinder] Cylinder032  label="Cilindro032"
  Angle = 360
  AttacherType = Attacher::AttachEngine3D
  Height = 10
  Placement = pos=(87.5,41.5,0) rot=(1,0,0;1.5708rad)
  Radius = 1.5
FEATURE [Part::MultiFuse] Fusion011
  Shapes = -> [Box017,Box018]
FEATURE [Part::Fillet] Fillet004
  Base = -> Fusion011
  Edges = 2 edges r=3: [Edge30,Edge32]
FEATURE [Part::MultiFuse] Fusion012
  Shapes = -> [Box016,Cylinder030,Cylinder032,Cylinder031]
FEATURE [Part::Cut] Cut013  label="colocador003"
  Base = -> Fillet004
  Placement = pos=(0,-73,0) rot=(0,0,1;0rad)
  Tool = -> Fusion012
FEATURE [Part::Feature] Cut003_solid  label="separador (Solid)"
  shape: bbox 7 x 6.062 x 25 mm, 9 faces (baked)
FEATURE [Part::Feature] Cut010_solid  label="colocador (Solid)"
  shape: bbox 15 x 2 x 40 mm, 21 faces (baked)
FEATURE [Mesh::Feature] Mesh001  label="separador (Solid) (Meshed)"
FEATURE [Mesh::Feature] Mesh002  label="colocador (Solid) (Meshed)"
FEATURE [Part::Cylinder] Cylinder033  label="Cilindro033"
  Angle = 360
  AttacherType = Attacher::AttachEngine3D
  Height = 30
  Placement = pos=(0,0,-2) rot=(0,0,1;0rad)
  Radius = 2
FEATURE [Part::Prism] Prism007  label="Prisma007"
  AttacherType = Attacher::AttachEngine3D
  Circumradius = 3.5
  Height = 5
  Polygon = 6
FEATURE [Part::Cut] Cut014  label="separador007"
  Base = -> Prism007
  Placement = pos=(62,-25,31) rot=(0,0,1;0rad)
  Tool = -> Cylinder033
FEATURE [Part::Cylinder] Cylinder034  label="Cilindro034"
  Angle = 360
  AttacherType = Attacher::AttachEngine3D
  Height = 30
  Placement = pos=(0,0,-2) rot=(0,0,1;0rad)
  Radius = 2
FEATURE [Part::Prism] Prism008  label="Prisma008"
  AttacherType = Attacher::AttachEngine3D
  Circumradius = 3.5
  Height = 5
  Polygon = 6
FEATURE [Part::Cut] Cut015  label="separador008"
  Base = -> Prism008
  Placement = pos=(110,-26,31) rot=(0,0,1;0rad)
  Tool = -> Cylinder034
FEATURE [Part::Cylinder] Cylinder035  label="Cilindro035"
  Angle = 360
  AttacherType = Attacher::AttachEngine3D
  Height = 30
  Placement = pos=(0,0,-2) rot=(0,0,1;0rad)
  Radius = 2
FEATURE [Part::Prism] Prism009  label="Prisma009"
  AttacherType = Attacher::AttachEngine3D
  Circumradius = 3.5
  Height = 5
  Polygon = 6
FEATURE [Part::Cut] Cut016  label="separador009"
  Base = -> Prism009
  Placement = pos=(105,25,31) rot=(0,0,1;0rad)
  Tool = -> Cylinder035
FEATURE [Part::Prism] Prism010  label="Prisma010"
  AttacherType = Attacher::AttachEngine3D
  Circumradius = 3.5
  Height = 5
  Polygon = 6
FEATURE [Part::Cylinder] Cylinder036  label="Cilindro036"
  Angle = 360
  AttacherType = Attacher::AttachEngine3D
  Height = 30
  Placement = pos=(0,0,-2) rot=(0,0,1;0rad)
  Radius = 2
FEATURE [Part::Cut] Cut017  label="separador010"
  Base = -> Prism010
  Placement = pos=(77,25,31) rot=(0,0,1;0rad)
  Tool = -> Cylinder036
FEATURE [Part::Prism] Prism011  label="Prisma011"
  AttacherType = Attacher::AttachEngine3D
  Circumradius = 3.5
  Height = 5
  Polygon = 6
FEATURE [Part::Cylinder] Cylinder037  label="Cilindro037"
  Angle = 360
  AttacherType = Attacher::AttachEngine3D
  Height = 30
  Placement = pos=(0,0,-2) rot=(0,0,1;0rad)
  Radius = 2
FEATURE [Part::Cut] Cut018  label="separador011"
  Base = -> Prism011
  Placement = pos=(15,15,31) rot=(0,0,1;0rad)
  Tool = -> Cylinder037
FEATURE [Part::Prism] Prism012  label="Prisma012"
  AttacherType = Attacher::AttachEngine3D
  Circumradius = 3.5
  Height = 5
  Polygon = 6
FEATURE [Part::Cylinder] Cylinder038  label="Cilindro038"
  Angle = 360
  AttacherType = Attacher::AttachEngine3D
  Height = 30
  Placement = pos=(0,0,-2) rot=(0,0,1;0rad)
  Radius = 2
FEATURE [Part::Cut] Cut019  label="separador012"
  Base = -> Prism012
  Placement = pos=(52,15,31) rot=(0,0,1;0rad)
  Tool = -> Cylinder038
FEATURE [Part::Cylinder] Cylinder039  label="Cilindro039"
  Angle = 360
  AttacherType = Attacher::AttachEngine3D
  Height = 30
  Placement = pos=(0,0,-2) rot=(0,0,1;0rad)
  Radius = 2
FEATURE [Part::Prism] Prism013  label="Prisma013"
  AttacherType = Attacher::AttachEngine3D
  Circumradius = 3.5
  Height = 5
  Polygon = 6
FEATURE [Part::Cut] Cut020  label="separador013"
  Base = -> Prism013
  Placement = pos=(52,-22,31) rot=(0,0,1;0rad)
  Tool = -> Cylinder039
FEATURE [Part::Prism] Prism014  label="Prisma014"
  AttacherType = Attacher::AttachEngine3D
  Circumradius = 3.5
  Height = 5
  Polygon = 6
FEATURE [Part::Cylinder] Cylinder040  label="Cilindro040"
  Angle = 360
  AttacherType = Attacher::AttachEngine3D
  Height = 30
  Placement = pos=(0,0,-2) rot=(0,0,1;0rad)
  Radius = 2
FEATURE [Part::Cut] Cut021  label="separador014"
  Base = -> Prism014
  Placement = pos=(15,-22,31) rot=(0,0,1;0rad)
  Tool = -> Cylinder040
FEATURE [Part::Feature] Cut021_solid  label="separadorSec"
  shape: bbox 7 x 6.062 x 5 mm, 9 faces (baked)
FEATURE [Part::Box] Box019  label="Cubo018"
  AttacherType = Attacher::AttachEngine3D
  Height = 2.5
  Length = 35
  Placement = pos=(113,-15,29) rot=(0,0,1;0rad)
  Width = 30
FEATURE [Part::Box] Box020  label="Cubo019"
  AttacherType = Attacher::AttachEngine3D
  Height = 2.5
  Length = 39
  Placement = pos=(115,-17,29) rot=(0,0,1;0rad)
  Width = 34
FEATURE [Part::MultiFuse] Fusion013
  Shapes = -> [Fillet,Box020]
FEATURE [Part::Cut] Cut022
  Base = -> Fusion013
  Tool = -> Box019
FEATURE [Part::Fillet] Fillet005  label="biselado"
  Base = -> Cut022
  Edges = 6 edges r=2: [Edge1,Edge3,Edge7,Edge15,Edge28,Edge34]
FEATURE [Part::Feature] path4522
  shape: bbox 6.314 x 4.985 x 2.279e-07 mm, 0 faces, 0 solids (baked)
FEATURE [Part::Feature] path4522001
  shape: bbox 2.322 x 1.012 x 2.279e-07 mm, 0 faces, 0 solids (baked)
FEATURE [Part::Feature] path4524
  shape: bbox 1.403 x 1.446 x 2.279e-07 mm, 0 faces, 0 solids (baked)
FEATURE [Part::Feature] path4526
  shape: bbox 6.076 x 4.985 x 2.279e-07 mm, 0 faces, 0 solids (baked)
FEATURE [Part::Feature] path4526001
  shape: bbox 2.174 x 0.6621 x 2.279e-07 mm, 0 faces, 0 solids (baked)
FEATURE [Part::Feature] path4528
  shape: bbox 6.274 x 4.977 x 2.279e-07 mm, 0 faces, 0 solids (baked)
FEATURE [Part::Feature] path4528001
  shape: bbox 2.371 x 0.6621 x 2.279e-07 mm, 0 faces, 0 solids (baked)
FEATURE [Part::Feature] path4530
  shape: bbox 6.274 x 4.977 x 2.279e-07 mm, 0 faces, 0 solids (baked)
FEATURE [Part::Feature] path4530001
  shape: bbox 2.371 x 0.6621 x 2.279e-07 mm, 0 faces, 0 solids (baked)
FEATURE [Part::Feature] path4532
  shape: bbox 1.956 x 4.977 x 2.279e-07 mm, 0 faces, 0 solids (baked)
FEATURE [Part::Feature] path4534
  shape: bbox 6.373 x 4.992 x 2.279e-07 mm, 0 faces, 0 solids (baked)
FEATURE [Part::Feature] path4534001
  shape: bbox 2.391 x 0.6849 x 2.279e-07 mm, 0 faces, 0 solids (baked)
FEATURE [Part::Feature] path4534002
  shape: bbox 2.391 x 0.6849 x 2.279e-07 mm, 0 faces, 0 solids (baked)
FEATURE [Part::Feature] path4536
  shape: bbox 6.076 x 4.985 x 2.279e-07 mm, 0 faces, 0 solids (baked)
FEATURE [Part::Feature] path4536001
  shape: bbox 2.174 x 0.6621 x 2.279e-07 mm, 0 faces, 0 solids (baked)
FEATURE [Part::Extrusion] Extrude
  Base = -> path4522
  Dir = (0,0,-1)
  DirMode = 2
  FaceMakerClass = Part::FaceMakerBullseye
  LengthFwd = 2
  LengthRev = 0
  Solid = true
  Symmetric = false
FEATURE [Part::Extrusion] Extrude001
  Base = -> path4522001
  Dir = (0,0,1)
  DirMode = 2
  FaceMakerClass = Part::FaceMakerBullseye
  LengthFwd = 2
  LengthRev = 0
  Placement = pos=(0,0,-2) rot=(0,0,1;0rad)
  Solid = true
  Symmetric = false
FEATURE [Part::Extrusion] Extrude002
  Base = -> path4524
  Dir = (0,0,-1)
  DirMode = 2
  FaceMakerClass = Part::FaceMakerBullseye
  LengthFwd = 2
  LengthRev = 0
  Solid = true
  Symmetric = false
FEATURE [Part::Extrusion] Extrude003
  Base = -> path4526
  Dir = (0,0,-1)
  DirMode = 2
  FaceMakerClass = Part::FaceMakerBullseye
  LengthFwd = 2
  LengthRev = 0
  Solid = true
  Symmetric = false
FEATURE [Part::Extrusion] Extrude004
  Base = -> path4526001
  Dir = (0,0,1)
  DirMode = 2
  FaceMakerClass = Part::FaceMakerBullseye
  LengthFwd = 2
  LengthRev = 0
  Placement = pos=(0,0,-2) rot=(0,0,1;0rad)
  Solid = true
  Symmetric = false
FEATURE [Part::Extrusion] Extrude005
  Base = -> path4528
  Dir = (0,0,-1)
  DirMode = 2
  FaceMakerClass = Part::FaceMakerBullseye
  LengthFwd = 2
  LengthRev = 0
  Solid = true
  Symmetric = false
FEATURE [Part::Extrusion] Extrude006
  Base = -> path4528001
  Dir = (0,0,1)
  DirMode = 2
  FaceMakerClass = Part::FaceMakerBullseye
  LengthFwd = 2
  LengthRev = 0
  Placement = pos=(0,0,-2) rot=(0,0,1;0rad)
  Solid = true
  Symmetric = false
FEATURE [Part::Extrusion] Extrude007
  Base = -> path4530
  Dir = (0,0,-1)
  DirMode = 2
  FaceMakerClass = Part::FaceMakerBullseye
  LengthFwd = 2
  LengthRev = 0
  Solid = true
  Symmetric = false
FEATURE [Part::Extrusion] Extrude008
  Base = -> path4530001
  Dir = (0,0,1)
  DirMode = 2
  FaceMakerClass = Part::FaceMakerBullseye
  LengthFwd = 2
  LengthRev = 0
  Placement = pos=(0,0,-2) rot=(0,0,1;0rad)
  Solid = true
  Symmetric = false
FEATURE [Part::Extrusion] Extrude009
  Base = -> path4532
  Dir = (0,0,-1)
  DirMode = 2
  FaceMakerClass = Part::FaceMakerBullseye
  LengthFwd = 2
  LengthRev = 0
  Solid = true
  Symmetric = false
FEATURE [Part::Extrusion] Extrude010
  Base = -> path4534
  Dir = (0,0,-1)
  DirMode = 2
  FaceMakerClass = Part::FaceMakerBullseye
  LengthFwd = 2
  LengthRev = 0
  Solid = true
  Symmetric = false
FEATURE [Part::Extrusion] Extrude011
  Base = -> path4534001
  Dir = (0,0,1)
  DirMode = 2
  FaceMakerClass = Part::FaceMakerBullseye
  LengthFwd = 2
  LengthRev = 0
  Placement = pos=(0,0,-2) rot=(0,0,1;0rad)
  Solid = true
  Symmetric = false
FEATURE [Part::Extrusion] Extrude012
  Base = -> path4534002
  Dir = (0,0,1)
  DirMode = 2
  FaceMakerClass = Part::FaceMakerBullseye
  LengthFwd = 2
  LengthRev = 0
  Placement = pos=(0,0,-2) rot=(0,0,1;0rad)
  Solid = true
  Symmetric = false
FEATURE [Part::Extrusion] Extrude013
  Base = -> path4536
  Dir = (0,0,-1)
  DirMode = 2
  FaceMakerClass = Part::FaceMakerBullseye
  LengthFwd = 2
  LengthRev = 0
  Solid = true
  Symmetric = false
FEATURE [Part::Extrusion] Extrude014
  Base = -> path4536001
  Dir = (0,0,1)
  DirMode = 2
  FaceMakerClass = Part::FaceMakerBullseye
  LengthFwd = 2
  LengthRev = 0
  Placement = pos=(0,0,-2) rot=(0,0,1;0rad)
  Solid = true
  Symmetric = false
FEATURE [Part::Cut] Cut023
  Base = -> Extrude
  Tool = -> Extrude001
FEATURE [Part::Cut] Cut024
  Base = -> Extrude003
  Tool = -> Extrude004
FEATURE [Part::Cut] Cut025
  Base = -> Extrude005
  Tool = -> Extrude006
FEATURE [Part::Cut] Cut026
  Base = -> Extrude007
  Tool = -> Extrude008
FEATURE [Part::MultiFuse] Fusion014
  Shapes = -> [Extrude011,Extrude012]
FEATURE [Part::Cut] Cut027
  Base = -> Extrude010
  Tool = -> Fusion014
FEATURE [Part::Cut] Cut028
  Base = -> Extrude013
  Tool = -> Extrude014
FEATURE [Part::MultiFuse] Fusion015  label="PARRIBA"
  Placement = pos=(0,43,33) rot=(0,0,1;0rad)
  Shapes = -> [Extrude002,Extrude009,Cut023,Cut024,Cut025,Cut026,Cut027,Cut028]
FEATURE [Part::FeaturePython] Scale  # Draft clone (typed FeaturePython)
  Fuse = false
  Objects = -> [Fusion015]
  Placement = pos=(9.32,6.53,32) rot=(0,0,1;0rad)
  Scale = (0.5,0.5,0.5)
FEATURE [Part::Cut] Cut029  label="SEGUNDOPISO"
  Base = -> Fillet005
  Tool = -> Scale
FEATURE [Mesh::Feature] Mesh  label="SEGUNDOPISO (Meshed)"
